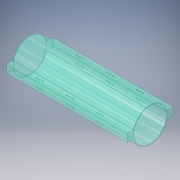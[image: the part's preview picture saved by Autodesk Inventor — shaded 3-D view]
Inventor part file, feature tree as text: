
AUTODESK INVENTOR PART (.ipt)
format: ipt  version: 2019 (Build 230136000, 136)  size: 157,184 bytes
history: native  units: in
note: dims shown in document units (in); Inventor stores cm internally (conversion verified against a paired STEP export)
features: extrude x3, sketch x3, mirror x2, plane x1
ambient origin geometry x8: Origin, YZ Plane, XZ Plane, XY Plane, X Axis, Y Axis, Z Axis, Center Point
bodies: Solid1 (feature_tree)
feature tree (9):
  extrude  "Extrusion1"  Depth=4.4882in
  extrude  "Extrusion2"  Depth=15.748in
  plane  "Work Plane1"
  mirror  "Mirror1"
  extrude  "Extrusion4"  Depth=15.748in TaperAngle=0.0deg
  mirror  "Mirror3"
  sketch  "Sketch1"  dims[d0=4.2913in d1=4.4882in]
  sketch  "Sketch2"  dims[d2=15.748in d3=0.0in d5=0.5118in]
  sketch  "Sketch3"  dims[d6=1.0236in d7=15.748in d8=0.0in d9=0.0in d27=15.748in d28=0.0in]
